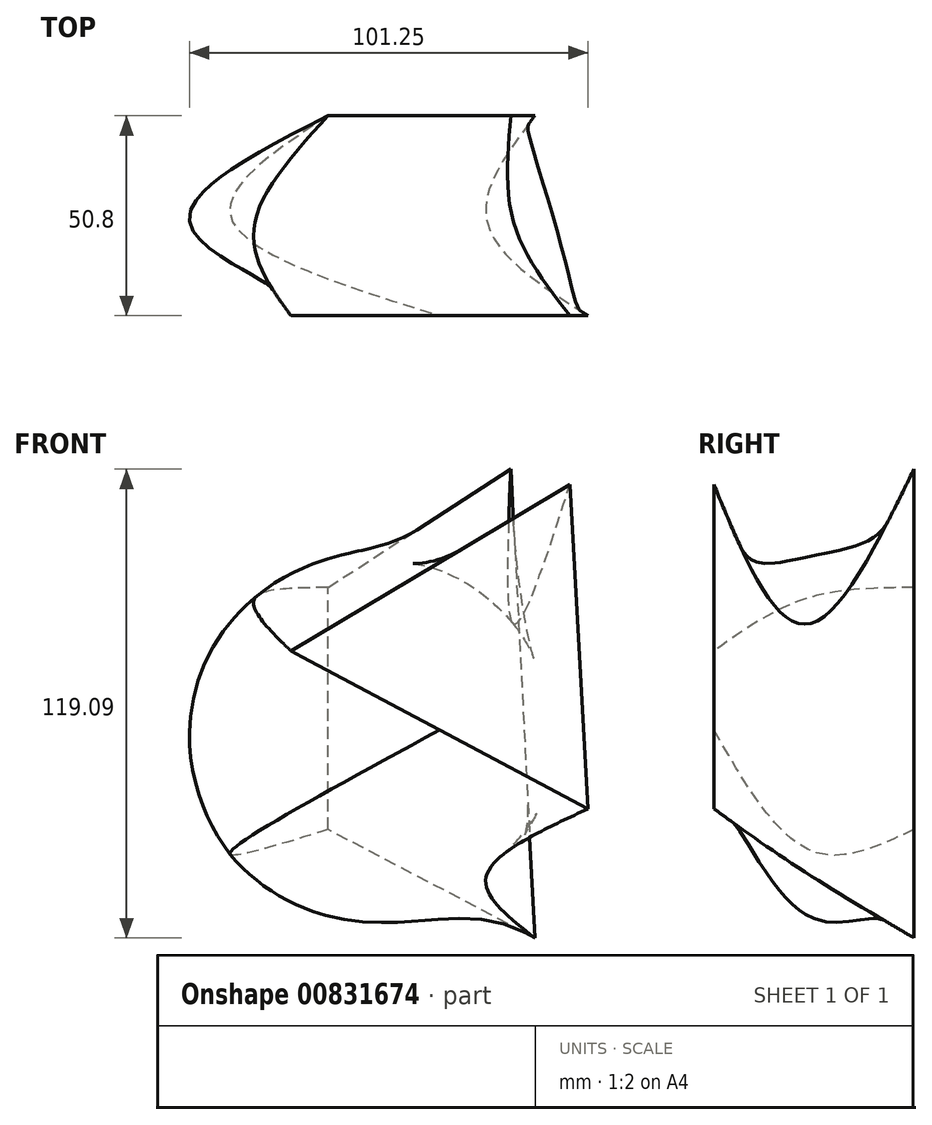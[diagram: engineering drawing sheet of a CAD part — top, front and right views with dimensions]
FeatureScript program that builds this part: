
annotation { "Feature Type Name" : "Feature", "Feature Type Description" : "" }
export const myFeature = defineFeature(function(context is Context, id is Id, definition is map)
    precondition{}
    {
        {
            var Q0;
            Q0=qCreatedBy(makeId("Front.planeOp"),FACE);
            var sketch = newSketch(context, id + "F0", { "sketchPlane" : qUnion([Q0])});
            skLineSegment(sketch, "E0", {"start": v(16.77, -72.87) * mm, "end": v(-35.77, -45.33) * mm});
            skLineSegment(sketch, "E1", {"start": v(-35.77, -45.33) * mm, "end": v(-35.77, 16.13) * mm});
            skLineSegment(sketch, "E2", {"start": v(-35.26, 30.92) * mm, "end": v(-35.77, 34.75) * mm});
            skLineSegment(sketch, "E3", {"start": v(-35.77, 16.13) * mm, "end": v(10.65, 46.22) * mm});
            skLineSegment(sketch, "E4", {"start": v(10.65, 46.22) * mm, "end": v(16.77, -72.87) * mm});
            skSolve(sketch);
        }
        {
            var Q0;
            Q0=qCreatedBy(makeId("Front.planeOp"),FACE);
            cPlane(context, id + "F1", {"entities" : qUnion([Q0]), "cplaneType" : CPlaneType.OFFSET, "offset" : 25.4 * mm, "width" : 152.4 * mm, "height" : 152.4 * mm});
        }
        {
            var Q0;
            Q0=qCreatedBy(id+"F1.planeOp",FACE);
            cPlane(context, id + "F2", {"entities" : qUnion([Q0]), "cplaneType" : CPlaneType.OFFSET, "offset" : 25.4 * mm, "width" : 152.4 * mm, "height" : 152.4 * mm});
        }
        {
            var Q0;
            Q0=qCreatedBy(id+"F2.planeOp",FACE);
            var sketch = newSketch(context, id + "F3", { "sketchPlane" : qUnion([Q0])});
            skLineSegment(sketch, "E5", {"start": v(25.7, 42.27) * mm, "end": v(-45.2, 0) * mm});
            skLineSegment(sketch, "E6", {"start": v(-45.2, 0) * mm, "end": v(30.28, -40.1) * mm});
            skLineSegment(sketch, "E7", {"start": v(30.28, -40.1) * mm, "end": v(25.7, 42.27) * mm});
            skSolve(sketch);
        }
        {
            var Q0;
            Q0=qCreatedBy(id+"F1.planeOp",FACE);
            var sketch = newSketch(context, id + "F4", { "sketchPlane" : qUnion([Q0])});
            skCircle(sketch, "E8", {"center": v(-24.8, -21.87) * mm, "radius": 46.14 * mm});
            skSolve(sketch);
        }
        {
            var Q0;
            Q0=makeQuery(id+"F0.imprint","IMPRINT",FACE,{"disambiguationData":[TD([[makeQuery(id+"F0.imprint","IMPRINT",EDGE,{"derivedFrom":sQuery(id+"F0.wireOp",EDGE,"E0")}),-1.0]])]});
            var Q1;
            Q1=makeQuery(id+"F4.imprint","IMPRINT",FACE,{"disambiguationData":[TD([[makeQuery(id+"F4.imprint","IMPRINT",EDGE,{"derivedFrom":sQuery(id+"F4.wireOp",EDGE,"E8")}),1.0]])]});
            var Q2;
            Q2=makeQuery(id+"F3.imprint","IMPRINT",FACE,{"disambiguationData":[TD([[makeQuery(id+"F3.imprint","IMPRINT",EDGE,{"derivedFrom":sQuery(id+"F3.wireOp",EDGE,"E5")}),1.0]])]});
            loft(context, id + "F5", {"sheetProfilesArray" : [{ "sheetProfileEntities" : qUnion([Q0]) }, { "sheetProfileEntities" : qUnion([Q1]) }, { "sheetProfileEntities" : qUnion([Q2]) }]});
        }
    });
